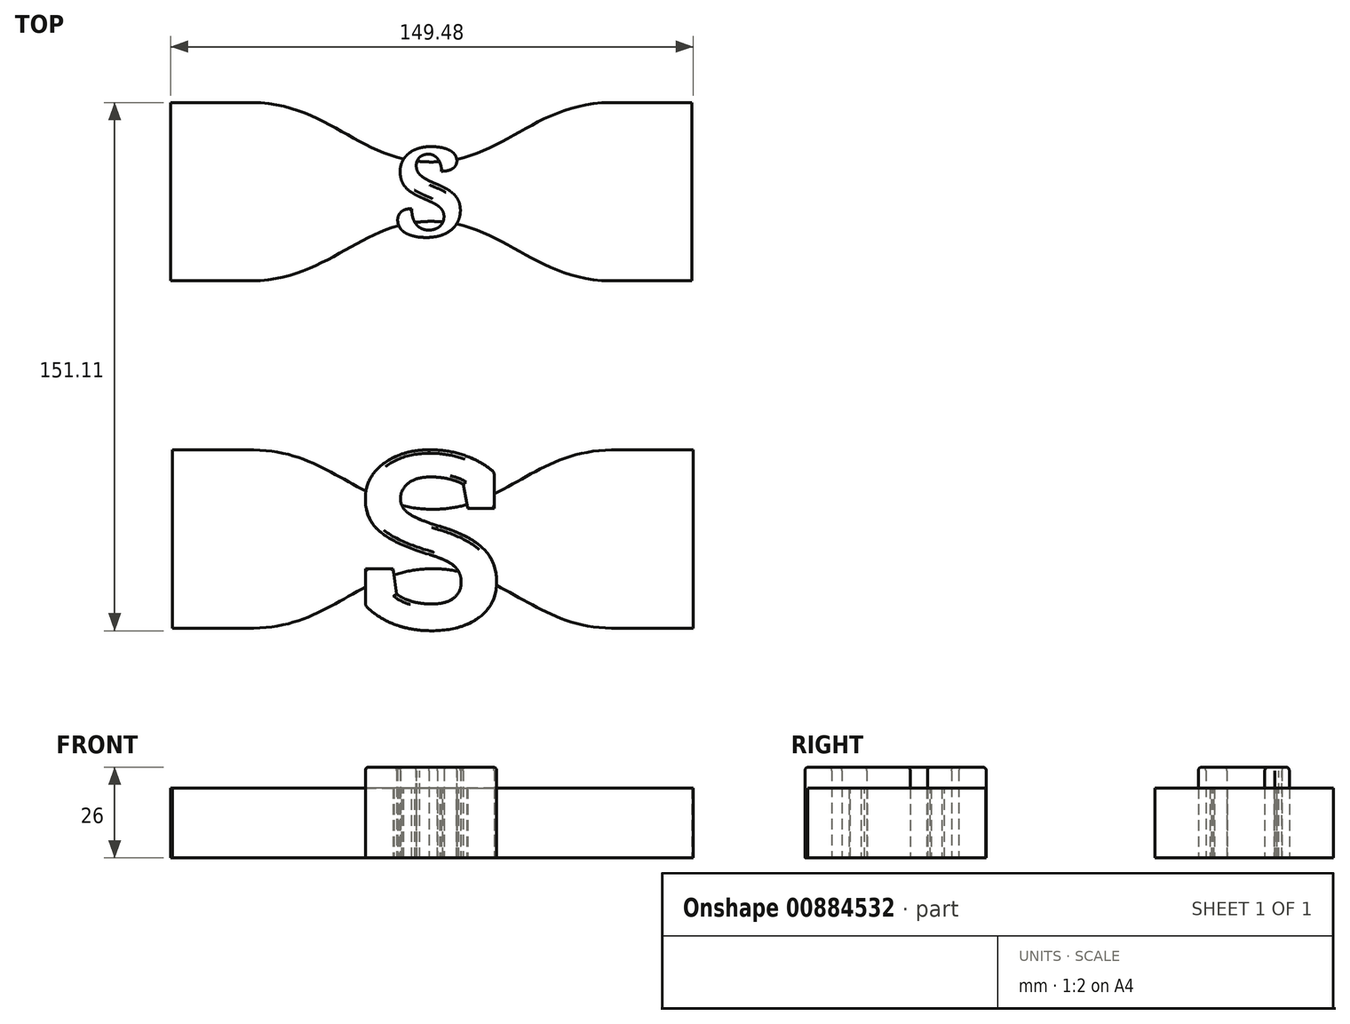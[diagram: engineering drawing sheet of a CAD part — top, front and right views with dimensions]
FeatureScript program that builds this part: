
annotation { "Feature Type Name" : "Feature", "Feature Type Description" : "" }
export const myFeature = defineFeature(function(context is Context, id is Id, definition is map)
    precondition{}
    {
        {
            var Q0;
            Q0=qCreatedBy(makeId("Top.planeOp"),FACE);
            var sketch = newSketch(context, id + "F0", { "sketchPlane" : qUnion([Q0])});
            skFitSpline(sketch, "E0.MirrorCS", {"points": [v(0, 8.5) * mm, v(-51.2, 25.5) * mm], "startDerivative": vector(-60.93, 0) * mm, "endDerivative": vector(-65.59, 0.6) * mm});
            skFitSpline(sketch, "E1.MirrorCS", {"points": [v(0, -8.5) * mm, v(-51.2, -25.5) * mm], "startDerivative": vector(-60.93, 0) * mm, "endDerivative": vector(-65.59, -0.6) * mm});
            skLineSegment(sketch, "E2", {"start": v(0, 8.5) * mm, "end": v(0, -8.5) * mm});
            skFitSpline(sketch, "E3.MirrorCS", {"points": [v(0, -8.5) * mm, v(51.2, -25.5) * mm], "startDerivative": vector(60.93, 0) * mm, "endDerivative": vector(65.59, -0.6) * mm});
            skFitSpline(sketch, "E4.MirrorCS", {"points": [v(0, 8.5) * mm, v(51.2, 25.5) * mm], "startDerivative": vector(60.93, 0) * mm, "endDerivative": vector(65.59, 0.6) * mm});
            skLineSegment(sketch, "E5", {"start": v(51.2, 25.5) * mm, "end": v(74.52, 25.5) * mm});
            skLineSegment(sketch, "E6.MirrorCS", {"start": v(51.2, -25.5) * mm, "end": v(74.52, -25.5) * mm});
            skLineSegment(sketch, "E7.MirrorCS", {"start": v(-51.2, 25.5) * mm, "end": v(-74.52, 25.5) * mm});
            skLineSegment(sketch, "E8.MirrorCS", {"start": v(-51.2, -25.5) * mm, "end": v(-74.52, -25.5) * mm});
            skPoint(sketch, "E9", {"position": v(88.57, 25.5) * mm});
            skFitSpline(sketch, "E10.MirrorCS", {"points": [v(0.44, -90.88) * mm, v(-50.76, -73.88) * mm], "startDerivative": vector(-60.93, 0) * mm, "endDerivative": vector(-65.59, 0.6) * mm});
            skFitSpline(sketch, "E11.MirrorCS", {"points": [v(0.44, -107.88) * mm, v(-50.76, -124.88) * mm], "startDerivative": vector(-60.93, 0) * mm, "endDerivative": vector(-65.59, -0.6) * mm});
            skLineSegment(sketch, "E12", {"start": v(0.44, -90.88) * mm, "end": v(0.44, -107.88) * mm});
            skFitSpline(sketch, "E13.MirrorCS", {"points": [v(0.44, -107.88) * mm, v(51.64, -124.88) * mm], "startDerivative": vector(60.93, 0) * mm, "endDerivative": vector(65.59, -0.6) * mm});
            skFitSpline(sketch, "E14.MirrorCS", {"points": [v(0.44, -90.88) * mm, v(51.64, -73.88) * mm], "startDerivative": vector(60.93, 0) * mm, "endDerivative": vector(65.59, 0.6) * mm});
            skLineSegment(sketch, "E15", {"start": v(51.64, -73.88) * mm, "end": v(74.96, -73.88) * mm});
            skLineSegment(sketch, "E16.MirrorCS", {"start": v(51.64, -124.88) * mm, "end": v(74.96, -124.88) * mm});
            skLineSegment(sketch, "E17.MirrorCS", {"start": v(-50.76, -73.88) * mm, "end": v(-74.08, -73.88) * mm});
            skLineSegment(sketch, "E18.MirrorCS", {"start": v(-50.76, -124.88) * mm, "end": v(-74.08, -124.88) * mm});
            skText(sketch, "E19", { "text": "S", "fontName": "RobotoSlab-Bold.ttf"});
            skLineSegment(sketch, "E20", {"start": v(-74.08, -73.88) * mm, "end": v(-74.08, -124.88) * mm});
            skLineSegment(sketch, "E21", {"start": v(74.96, -73.88) * mm, "end": v(74.96, -124.88) * mm});
            skFitSpline(sketch, "E22.MirrorCS", {"points": [v(-1.58, 91.78) * mm, v(-52.78, 108.78) * mm], "startDerivative": vector(-60.93, 0) * mm, "endDerivative": vector(-65.59, 0.6) * mm});
            skFitSpline(sketch, "E23.MirrorCS", {"points": [v(-1.58, 74.78) * mm, v(-52.78, 57.78) * mm], "startDerivative": vector(-60.93, 0) * mm, "endDerivative": vector(-65.59, -0.6) * mm});
            skLineSegment(sketch, "E24", {"start": v(-1.58, 91.78) * mm, "end": v(-1.58, 74.78) * mm});
            skFitSpline(sketch, "E25.MirrorCS", {"points": [v(-1.58, 74.78) * mm, v(49.61, 57.78) * mm], "startDerivative": vector(60.93, 0) * mm, "endDerivative": vector(65.59, -0.6) * mm});
            skFitSpline(sketch, "E26.MirrorCS", {"points": [v(-1.58, 91.78) * mm, v(49.61, 108.78) * mm], "startDerivative": vector(60.93, 0) * mm, "endDerivative": vector(65.59, 0.6) * mm});
            skLineSegment(sketch, "E27", {"start": v(49.61, 108.78) * mm, "end": v(72.94, 108.78) * mm});
            skLineSegment(sketch, "E28.MirrorCS", {"start": v(49.61, 57.78) * mm, "end": v(72.94, 57.78) * mm});
            skLineSegment(sketch, "E29.MirrorCS", {"start": v(-52.78, 108.78) * mm, "end": v(-76.1, 108.78) * mm});
            skLineSegment(sketch, "E30.MirrorCS", {"start": v(-52.78, 57.78) * mm, "end": v(-76.1, 57.78) * mm});
            skLineSegment(sketch, "E31", {"start": v(86.99, 108.78) * mm, "end": v(141.68, 108.78) * mm, "construction": true});
            skLineSegment(sketch, "E32", {"start": v(84.7, 57.78) * mm, "end": v(147.8, 57.78) * mm, "construction": true});
            skPoint(sketch, "E33", {"position": v(86.99, 108.78) * mm});
            skText(sketch, "E34", { "text": "S", "fontName": "NotoSerif-Bold.ttf"});
            skText(sketch, "E35", { "text": "S", "fontName": "NotoSerif-Bold.ttf"});
            skLineSegment(sketch, "E36", {"start": v(-74.52, 25.5) * mm, "end": v(-74.52, -25.5) * mm});
            skLineSegment(sketch, "E37", {"start": v(74.52, 25.5) * mm, "end": v(74.52, -25.5) * mm});
            const initialGuessF0  = {"E19": [-0.02219, -0.12488, 1, 0, 0.051], "E34": [0.0847, 0.05778, 1, 0, 0.051], "E35": [-0.01064, -0.01275, 1, 0, 0.0255]};
            skSetInitialGuess(sketch, initialGuessF0);
            skSolve(sketch);
        }
        {
            var Q0;
            {var subQ13=sQuery(id+"F0.wireOp",EDGE,"E7.MirrorCS");Q0=makeQuery(id+"F0.imprint","IMPRINT",FACE,{"disambiguationData":[TD([[makeQuery(id+"F0.imprint","IMPRINT",EDGE,{"derivedFrom":subQ13}),1.0]])]});}
            var Q1;
            {var subQ0=sQuery(id+"F0.wireOp",EDGE,"E5");Q1=makeQuery(id+"F0.imprint","IMPRINT",FACE,{"disambiguationData":[TD([[makeQuery(id+"F0.imprint","IMPRINT",EDGE,{"derivedFrom":subQ0}),-1.0]])]});}
            var Q2;
            {var subQ0=sQuery(id+"F0.wireOp",EDGE,"E35.sketch_text.stroke-44");Q2=makeQuery(id+"F0.imprint","IMPRINT",FACE,{"disambiguationData":[TD([[makeQuery(id+"F0.imprint","IMPRINT",EDGE,{"derivedFrom":subQ0}),1.0]])]});}
            var Q3;
            {var subQ0=sQuery(id+"F0.wireOp",EDGE,"E35.sketch_text.stroke-16");Q3=makeQuery(id+"F0.imprint","IMPRINT",FACE,{"disambiguationData":[TD([[makeQuery(id+"F0.imprint","IMPRINT",EDGE,{"derivedFrom":subQ0}),1.0]])]});}
            var Q4;
            {var subQ4=sQuery(id+"F0.wireOp",EDGE,"E17.MirrorCS");Q4=makeQuery(id+"F0.imprint","IMPRINT",FACE,{"disambiguationData":[TD([[makeQuery(id+"F0.imprint","IMPRINT",EDGE,{"derivedFrom":subQ4}),1.0]])]});}
            var Q5;
            {var subQ10=sQuery(id+"F0.wireOp",EDGE,"E15");Q5=makeQuery(id+"F0.imprint","IMPRINT",FACE,{"disambiguationData":[TD([[makeQuery(id+"F0.imprint","IMPRINT",EDGE,{"derivedFrom":subQ10}),-1.0]])]});}
            var Q6;
            {var subQ3=sQuery(id+"F0.wireOp",EDGE,"E19.sketch_text.stroke-22");var subQ5=sQuery(id+"F0.wireOp",EDGE,"E19.sketch_text.stroke-21");var subQ6=makeQuery(id+"F0.imprint","INTERSECT",VERTEX,{"derivedFrom":[subQ5,subQ3]});Q6=makeQuery(id+"F0.imprint","IMPRINT",FACE,{"disambiguationData":[TD([[makeQuery(id+"F0.imprint","IMPRINT",EDGE,{"disambiguationData":[TD([[subQ6,1.0]])],"derivedFrom":subQ5}),1.0]])]});}
            var Q7;
            {var subQ3=sQuery(id+"F0.wireOp",EDGE,"E19.sketch_text.stroke-6");var subQ5=sQuery(id+"F0.wireOp",EDGE,"E19.sketch_text.stroke-7");var subQ7=makeQuery(id+"F0.imprint","INTERSECT",VERTEX,{"derivedFrom":[subQ3,subQ5]});Q7=makeQuery(id+"F0.imprint","IMPRINT",FACE,{"disambiguationData":[TD([[makeQuery(id+"F0.imprint","IMPRINT",EDGE,{"disambiguationData":[TD([[subQ7,1.0]])],"derivedFrom":subQ3}),1.0]])]});}
            extrude(context, id + "F1", {"entities" : qUnion([Q0, Q1, Q2, Q3, Q4, Q5, Q6, Q7]), "depth" : 20 * mm, "offsetDistance" : 25 * mm});
        }
        {
            var Q0;
            {var subQ13=sQuery(id+"F0.wireOp",EDGE,"E35.sketch_text.stroke-26");Q0=makeQuery(id+"F0.imprint","IMPRINT",FACE,{"disambiguationData":[TD([[makeQuery(id+"F0.imprint","IMPRINT",EDGE,{"derivedFrom":subQ13}),-1.0]])]});}
            var Q1;
            {var subQ13=sQuery(id+"F0.wireOp",EDGE,"E35.sketch_text.stroke-20");Q1=makeQuery(id+"F0.imprint","IMPRINT",FACE,{"disambiguationData":[TD([[makeQuery(id+"F0.imprint","IMPRINT",EDGE,{"derivedFrom":subQ13}),-1.0]])]});}
            var Q2;
            {var subQ12=sQuery(id+"F0.wireOp",EDGE,"E35.sketch_text.stroke-16");Q2=makeQuery(id+"F0.imprint","IMPRINT",FACE,{"disambiguationData":[TD([[makeQuery(id+"F0.imprint","IMPRINT",EDGE,{"derivedFrom":subQ12}),-1.0]])]});}
            var Q3;
            Q3=makeQuery(id+"F0.imprint","IMPRINT",FACE,{"disambiguationData":[TD([[makeQuery(id+"F0.imprint","IMPRINT",EDGE,{"derivedFrom":sQuery(id+"F0.wireOp",EDGE,"E35.sketch_text.stroke-0")}),-1.0]])]});
            var Q4;
            {var subQ0=sQuery(id+"F0.wireOp",EDGE,"E35.sketch_text.stroke-4");Q4=makeQuery(id+"F0.imprint","IMPRINT",FACE,{"disambiguationData":[TD([[makeQuery(id+"F0.imprint","IMPRINT",EDGE,{"derivedFrom":subQ0}),-1.0]])]});}
            var Q5;
            {var subQ0=sQuery(id+"F0.wireOp",EDGE,"E35.sketch_text.stroke-32");Q5=makeQuery(id+"F0.imprint","IMPRINT",FACE,{"disambiguationData":[TD([[makeQuery(id+"F0.imprint","IMPRINT",EDGE,{"derivedFrom":subQ0}),-1.0]])]});}
            var Q6;
            {var subQ5=sQuery(id+"F0.wireOp",EDGE,"E19.sketch_text.stroke-0");Q6=makeQuery(id+"F0.imprint","IMPRINT",FACE,{"disambiguationData":[TD([[makeQuery(id+"F0.imprint","IMPRINT",EDGE,{"derivedFrom":subQ5}),-1.0]])]});}
            var Q7;
            {var subQ7=sQuery(id+"F0.wireOp",EDGE,"E19.sketch_text.stroke-2");Q7=makeQuery(id+"F0.imprint","IMPRINT",FACE,{"disambiguationData":[TD([[makeQuery(id+"F0.imprint","IMPRINT",EDGE,{"derivedFrom":subQ7}),-1.0]])]});}
            var Q8;
            {var subQ5=sQuery(id+"F0.wireOp",EDGE,"E19.sketch_text.stroke-23");Q8=makeQuery(id+"F0.imprint","IMPRINT",FACE,{"disambiguationData":[TD([[makeQuery(id+"F0.imprint","IMPRINT",EDGE,{"derivedFrom":subQ5}),-1.0]])]});}
            var Q9;
            {var subQ0=sQuery(id+"F0.wireOp",EDGE,"E19.sketch_text.stroke-8");Q9=makeQuery(id+"F0.imprint","IMPRINT",FACE,{"disambiguationData":[TD([[makeQuery(id+"F0.imprint","IMPRINT",EDGE,{"derivedFrom":subQ0}),-1.0]])]});}
            var Q10;
            {var subQ7=sQuery(id+"F0.wireOp",EDGE,"E19.sketch_text.stroke-11");Q10=makeQuery(id+"F0.imprint","IMPRINT",FACE,{"disambiguationData":[TD([[makeQuery(id+"F0.imprint","IMPRINT",EDGE,{"derivedFrom":subQ7}),-1.0]])]});}
            var Q11;
            {var subQ5=sQuery(id+"F0.wireOp",EDGE,"E19.sketch_text.stroke-15");Q11=makeQuery(id+"F0.imprint","IMPRINT",FACE,{"disambiguationData":[TD([[makeQuery(id+"F0.imprint","IMPRINT",EDGE,{"derivedFrom":subQ5}),-1.0]])]});}
            extrude(context, id + "F2", {"entities" : qUnion([Q0, Q1, Q2, Q3, Q4, Q5, Q6, Q7, Q8, Q9, Q10, Q11]), "depth" : 26 * mm, "offsetDistance" : 25 * mm});
        }
        {
            var Q0;
            Q0=makeQuery(id+"F2.opExtrude","SWEPT_EDGE",EDGE,{"disambiguationData":[OSD([sQuery(id+"F0.wireOp",EDGE,"E35.sketch_text.stroke-35"),sQuery(id+"F0.wireOp",EDGE,"E35.sketch_text.stroke-36")])]});
            var Q1;
            Q1=makeQuery(id+"F2.opExtrude","SWEPT_EDGE",EDGE,{"disambiguationData":[OSD([sQuery(id+"F0.wireOp",EDGE,"E35.sketch_text.stroke-7"),sQuery(id+"F0.wireOp",EDGE,"E35.sketch_text.stroke-8")])]});
            var Q2;
            Q2=makeQuery(id+"F2.opExtrude","SWEPT_EDGE",EDGE,{"disambiguationData":[OSD([sQuery(id+"F0.wireOp",EDGE,"E19.sketch_text.stroke-0"),sQuery(id+"F0.wireOp",EDGE,"E19.sketch_text.stroke-1")])]});
            var Q3;
            Q3=makeQuery(id+"F2.opExtrude","SWEPT_EDGE",EDGE,{"disambiguationData":[OSD([sQuery(id+"F0.wireOp",EDGE,"E19.sketch_text.stroke-0"),sQuery(id+"F0.wireOp",EDGE,"E19.sketch_text.stroke-29")])]});
            var Q4;
            Q4=makeQuery(id+"F2.opExtrude","SWEPT_EDGE",EDGE,{"disambiguationData":[OSD([sQuery(id+"F0.wireOp",EDGE,"E19.sketch_text.stroke-14"),sQuery(id+"F0.wireOp",EDGE,"E19.sketch_text.stroke-15")])]});
            var Q5;
            Q5=makeQuery(id+"F2.opExtrude","SWEPT_EDGE",EDGE,{"disambiguationData":[OSD([sQuery(id+"F0.wireOp",EDGE,"E19.sketch_text.stroke-15"),sQuery(id+"F0.wireOp",EDGE,"E19.sketch_text.stroke-16")])]});
            var Q6;
            Q6=makeQuery(id+"F2.opExtrude","SWEPT_EDGE",EDGE,{"disambiguationData":[OSD([sQuery(id+"F0.wireOp",EDGE,"E19.sketch_text.stroke-13"),sQuery(id+"F0.wireOp",EDGE,"E19.sketch_text.stroke-14")])]});
            var Q7;
            Q7=makeQuery(id+"F2.opExtrude","SWEPT_EDGE",EDGE,{"disambiguationData":[OSD([sQuery(id+"F0.wireOp",EDGE,"E19.sketch_text.stroke-28"),sQuery(id+"F0.wireOp",EDGE,"E19.sketch_text.stroke-29")])]});
            fillet(context, id + "F3", {"entities" : qUnion([Q0, Q1, Q2, Q3, Q4, Q5, Q6, Q7]), "radius" : 1 * mm, "tangentPropagation" : true, "allowEdgeOverflow" : false});
        }
        {
            var Q0;
            Q0=makeQuery(id+"F2.opExtrude","CAP_FACE",FACE,{"disambiguationData":[OSD([sQuery(id+"F0.wireOp",EDGE,"E35.sketch_text.stroke-0"),sQuery(id+"F0.wireOp",EDGE,"E35.sketch_text.stroke-1"),sQuery(id+"F0.wireOp",EDGE,"E35.sketch_text.stroke-2"),sQuery(id+"F0.wireOp",EDGE,"E35.sketch_text.stroke-3"),sQuery(id+"F0.wireOp",EDGE,"E35.sketch_text.stroke-4"),sQuery(id+"F0.wireOp",EDGE,"E35.sketch_text.stroke-5"),sQuery(id+"F0.wireOp",EDGE,"E35.sketch_text.stroke-6"),sQuery(id+"F0.wireOp",EDGE,"E35.sketch_text.stroke-7"),sQuery(id+"F0.wireOp",EDGE,"E35.sketch_text.stroke-8"),sQuery(id+"F0.wireOp",EDGE,"E35.sketch_text.stroke-9"),sQuery(id+"F0.wireOp",EDGE,"E35.sketch_text.stroke-10"),sQuery(id+"F0.wireOp",EDGE,"E35.sketch_text.stroke-11"),sQuery(id+"F0.wireOp",EDGE,"E35.sketch_text.stroke-12"),sQuery(id+"F0.wireOp",EDGE,"E35.sketch_text.stroke-13"),sQuery(id+"F0.wireOp",EDGE,"E35.sketch_text.stroke-14"),sQuery(id+"F0.wireOp",EDGE,"E35.sketch_text.stroke-15"),sQuery(id+"F0.wireOp",EDGE,"E35.sketch_text.stroke-16"),sQuery(id+"F0.wireOp",EDGE,"E35.sketch_text.stroke-17"),sQuery(id+"F0.wireOp",EDGE,"E35.sketch_text.stroke-18"),sQuery(id+"F0.wireOp",EDGE,"E35.sketch_text.stroke-19"),sQuery(id+"F0.wireOp",EDGE,"E35.sketch_text.stroke-20"),sQuery(id+"F0.wireOp",EDGE,"E35.sketch_text.stroke-21"),sQuery(id+"F0.wireOp",EDGE,"E35.sketch_text.stroke-22"),sQuery(id+"F0.wireOp",EDGE,"E35.sketch_text.stroke-23"),sQuery(id+"F0.wireOp",EDGE,"E35.sketch_text.stroke-24"),sQuery(id+"F0.wireOp",EDGE,"E35.sketch_text.stroke-25"),sQuery(id+"F0.wireOp",EDGE,"E35.sketch_text.stroke-26"),sQuery(id+"F0.wireOp",EDGE,"E35.sketch_text.stroke-27"),sQuery(id+"F0.wireOp",EDGE,"E35.sketch_text.stroke-28"),sQuery(id+"F0.wireOp",EDGE,"E35.sketch_text.stroke-29"),sQuery(id+"F0.wireOp",EDGE,"E35.sketch_text.stroke-30"),sQuery(id+"F0.wireOp",EDGE,"E35.sketch_text.stroke-31"),sQuery(id+"F0.wireOp",EDGE,"E35.sketch_text.stroke-32"),sQuery(id+"F0.wireOp",EDGE,"E35.sketch_text.stroke-33"),sQuery(id+"F0.wireOp",EDGE,"E35.sketch_text.stroke-34"),sQuery(id+"F0.wireOp",EDGE,"E35.sketch_text.stroke-35"),sQuery(id+"F0.wireOp",EDGE,"E35.sketch_text.stroke-36"),sQuery(id+"F0.wireOp",EDGE,"E35.sketch_text.stroke-37"),sQuery(id+"F0.wireOp",EDGE,"E35.sketch_text.stroke-38"),sQuery(id+"F0.wireOp",EDGE,"E35.sketch_text.stroke-39"),sQuery(id+"F0.wireOp",EDGE,"E35.sketch_text.stroke-40"),sQuery(id+"F0.wireOp",EDGE,"E35.sketch_text.stroke-41"),sQuery(id+"F0.wireOp",EDGE,"E35.sketch_text.stroke-42"),sQuery(id+"F0.wireOp",EDGE,"E35.sketch_text.stroke-43"),sQuery(id+"F0.wireOp",EDGE,"E35.sketch_text.stroke-44"),sQuery(id+"F0.wireOp",EDGE,"E35.sketch_text.stroke-45"),sQuery(id+"F0.wireOp",EDGE,"E35.sketch_text.stroke-46"),sQuery(id+"F0.wireOp",EDGE,"E35.sketch_text.stroke-47"),sQuery(id+"F0.wireOp",EDGE,"E35.sketch_text.stroke-48"),sQuery(id+"F0.wireOp",EDGE,"E35.sketch_text.stroke-49"),sQuery(id+"F0.wireOp",EDGE,"E35.sketch_text.stroke-50"),sQuery(id+"F0.wireOp",EDGE,"E35.sketch_text.stroke-51"),sQuery(id+"F0.wireOp",EDGE,"E35.sketch_text.stroke-52"),sQuery(id+"F0.wireOp",EDGE,"E35.sketch_text.stroke-53"),sQuery(id+"F0.wireOp",EDGE,"E35.sketch_text.stroke-54"),sQuery(id+"F0.wireOp",EDGE,"E35.sketch_text.stroke-55")])],"isStart":false});
            var Q1;
            Q1=makeQuery(id+"F2.opExtrude","CAP_FACE",FACE,{"disambiguationData":[OSD([sQuery(id+"F0.wireOp",EDGE,"E19.sketch_text.stroke-0"),sQuery(id+"F0.wireOp",EDGE,"E19.sketch_text.stroke-1"),sQuery(id+"F0.wireOp",EDGE,"E19.sketch_text.stroke-2"),sQuery(id+"F0.wireOp",EDGE,"E19.sketch_text.stroke-3"),sQuery(id+"F0.wireOp",EDGE,"E19.sketch_text.stroke-4"),sQuery(id+"F0.wireOp",EDGE,"E19.sketch_text.stroke-5"),sQuery(id+"F0.wireOp",EDGE,"E19.sketch_text.stroke-6"),sQuery(id+"F0.wireOp",EDGE,"E19.sketch_text.stroke-7"),sQuery(id+"F0.wireOp",EDGE,"E19.sketch_text.stroke-8"),sQuery(id+"F0.wireOp",EDGE,"E19.sketch_text.stroke-9"),sQuery(id+"F0.wireOp",EDGE,"E19.sketch_text.stroke-10"),sQuery(id+"F0.wireOp",EDGE,"E19.sketch_text.stroke-11"),sQuery(id+"F0.wireOp",EDGE,"E19.sketch_text.stroke-12"),sQuery(id+"F0.wireOp",EDGE,"E19.sketch_text.stroke-13"),sQuery(id+"F0.wireOp",EDGE,"E19.sketch_text.stroke-14"),sQuery(id+"F0.wireOp",EDGE,"E19.sketch_text.stroke-15"),sQuery(id+"F0.wireOp",EDGE,"E19.sketch_text.stroke-16"),sQuery(id+"F0.wireOp",EDGE,"E19.sketch_text.stroke-17"),sQuery(id+"F0.wireOp",EDGE,"E19.sketch_text.stroke-18"),sQuery(id+"F0.wireOp",EDGE,"E19.sketch_text.stroke-19"),sQuery(id+"F0.wireOp",EDGE,"E19.sketch_text.stroke-20"),sQuery(id+"F0.wireOp",EDGE,"E19.sketch_text.stroke-21"),sQuery(id+"F0.wireOp",EDGE,"E19.sketch_text.stroke-22"),sQuery(id+"F0.wireOp",EDGE,"E19.sketch_text.stroke-23"),sQuery(id+"F0.wireOp",EDGE,"E19.sketch_text.stroke-24"),sQuery(id+"F0.wireOp",EDGE,"E19.sketch_text.stroke-25"),sQuery(id+"F0.wireOp",EDGE,"E19.sketch_text.stroke-26"),sQuery(id+"F0.wireOp",EDGE,"E19.sketch_text.stroke-27"),sQuery(id+"F0.wireOp",EDGE,"E19.sketch_text.stroke-28"),sQuery(id+"F0.wireOp",EDGE,"E19.sketch_text.stroke-29")])],"isStart":false});
            fillet(context, id + "F4", {"entities" : qUnion([Q0, Q1]), "radius" : 1 * mm, "tangentPropagation" : true, "allowEdgeOverflow" : false});
        }
    });
